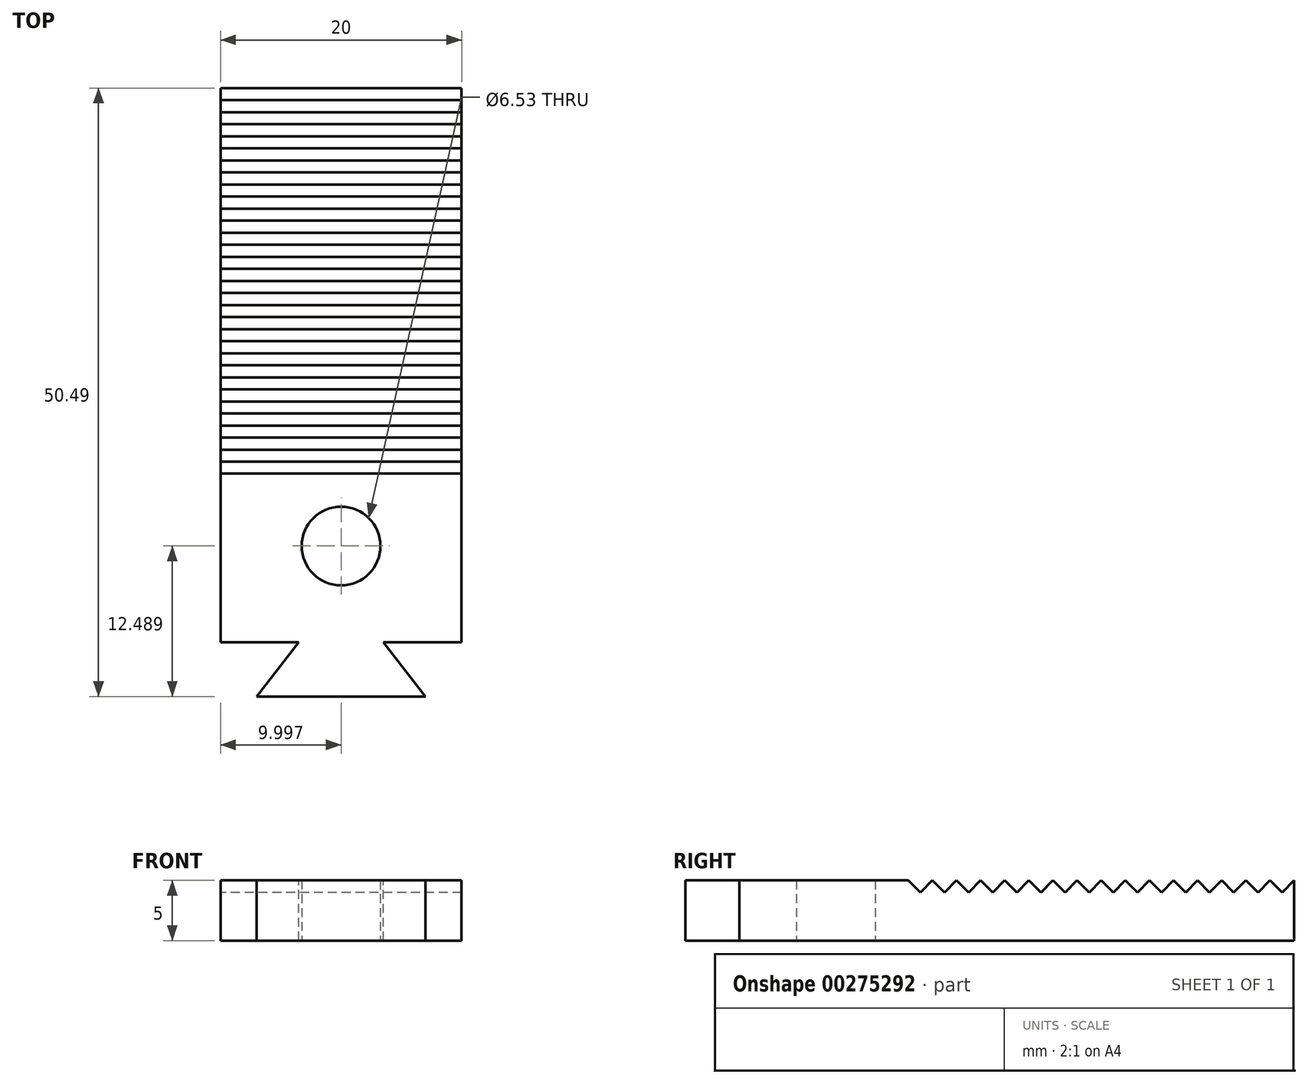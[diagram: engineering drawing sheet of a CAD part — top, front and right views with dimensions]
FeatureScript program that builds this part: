
annotation { "Feature Type Name" : "Feature", "Feature Type Description" : "" }
export const myFeature = defineFeature(function(context is Context, id is Id, definition is map)
    precondition{}
    {
        {
            var Q0;
            Q0=qCreatedBy(makeId("Top.planeOp"),FACE);
            var sketch = newSketch(context, id + "F0", { "sketchPlane" : qUnion([Q0])});
            skLineSegment(sketch, "E0.bottom", {"start": v(-15.11, 35.05) * mm, "end": v(4.89, 35.05) * mm});
            skLineSegment(sketch, "E0.top", {"start": v(-15.11, -20.95) * mm, "end": v(4.89, -20.95) * mm});
            skLineSegment(sketch, "E0.left", {"start": v(-15.11, 35.05) * mm, "end": v(-15.11, -20.95) * mm});
            skLineSegment(sketch, "E0.right", {"start": v(4.89, 35.05) * mm, "end": v(4.89, -20.95) * mm});
            skSolve(sketch);
        }
        {
            var Q0;
            Q0=makeQuery(id+"F0.imprint","IMPRINT",FACE,{"disambiguationData":[TD([[makeQuery(id+"F0.imprint","IMPRINT",EDGE,{"derivedFrom":sQuery(id+"F0.wireOp",EDGE,"E0.bottom")}),-1.0]])]});
            extrude(context, id + "F1", {"entities" : qUnion([Q0]), "depth" : 5 * mm});
        }
        {
            var Q0;
            Q0=makeQuery(id+"F1.opExtrude","CAP_FACE",FACE,{"disambiguationData":[OSD([sQuery(id+"F0.wireOp",EDGE,"E0.bottom"),sQuery(id+"F0.wireOp",EDGE,"E0.top"),sQuery(id+"F0.wireOp",EDGE,"E0.left"),sQuery(id+"F0.wireOp",EDGE,"E0.right")])],"isStart":false});
            var sketch = newSketch(context, id + "F2", { "sketchPlane" : qUnion([Q0])});
            skLineSegment(sketch, "E1.bottom", {"start": v(-15.11, -20.95) * mm, "end": v(4.89, -20.95) * mm});
            skLineSegment(sketch, "E1.top", {"start": v(-15.11, -10.95) * mm, "end": v(4.89, -10.95) * mm});
            skLineSegment(sketch, "E1.left", {"start": v(-15.11, -20.95) * mm, "end": v(-15.11, -10.95) * mm});
            skLineSegment(sketch, "E1.right", {"start": v(4.89, -20.95) * mm, "end": v(4.89, -10.95) * mm});
            skSolve(sketch);
        }
        {
            var Q0;
            Q0=makeQuery(id+"F2.imprint","IMPRINT",FACE,{"disambiguationData":[TD([[makeQuery(id+"F2.imprint","IMPRINT",EDGE,{"derivedFrom":sQuery(id+"F2.wireOp",EDGE,"E1.bottom")}),1.0]])]});
            extrude(context, id + "F3", {"entities" : qUnion([Q0]), "operationType" : NewBodyOperationType.ADD, "depth" : 45 * mm});
        }
        {
            var Q0;
            Q0=makeQuery(id+"F1.opExtrude","CAP_FACE",FACE,{"disambiguationData":[OSD([sQuery(id+"F0.wireOp",EDGE,"E0.bottom"),sQuery(id+"F0.wireOp",EDGE,"E0.top"),sQuery(id+"F0.wireOp",EDGE,"E0.left"),sQuery(id+"F0.wireOp",EDGE,"E0.right")])],"isStart":true});
            var sketch = newSketch(context, id + "F4", { "sketchPlane" : qUnion([Q0])});
            skPoint(sketch, "E2", {"position": v(-5.11, 2.95) * mm});
            skCircle(sketch, "E3.cCircle", {"center": v(-5.11, 2.95) * mm, "radius": 5.45 * mm, "construction": true});
            skLineSegment(sketch, "E3.0", {"start": v(-11.4, 2.95) * mm, "end": v(-8.26, 8.4) * mm});
            skLineSegment(sketch, "E3.1", {"start": v(-8.26, 8.4) * mm, "end": v(-1.97, 8.4) * mm});
            skLineSegment(sketch, "E3.2", {"start": v(-1.97, 8.4) * mm, "end": v(1.18, 2.95) * mm});
            skLineSegment(sketch, "E3.3", {"start": v(1.18, 2.95) * mm, "end": v(-1.97, -2.5) * mm});
            skLineSegment(sketch, "E3.4", {"start": v(-1.97, -2.5) * mm, "end": v(-8.26, -2.5) * mm});
            skLineSegment(sketch, "E3.5", {"start": v(-8.26, -2.5) * mm, "end": v(-11.4, 2.95) * mm});
            skPoint(sketch, "E3.0.midPoint", {"position": v(-9.83, 5.68) * mm});
            skSolve(sketch);
        }
        {
            var Q0;
            Q0=sQuery(id+"F4.wireOp",VERTEX,"E2");
            var Q1;
            Q1=makeQuery(id+"F1.opExtrude","SWEPT_BODY",BODY,{"disambiguationData":[OSD([sQuery(id+"F0.wireOp",EDGE,"E0.bottom"),sQuery(id+"F0.wireOp",EDGE,"E0.top"),sQuery(id+"F0.wireOp",EDGE,"E0.left"),sQuery(id+"F0.wireOp",EDGE,"E0.right")])]});
            hole(context, id + "F5", {"style" : HoleStyle.SIMPLE, "endStyle" : HoleEndStyle.THROUGH, "holeDiameter" : 6.53 * mm, "tappedDepth" : 12 * mm, "tapClearance" : 3, "locations" : qUnion([Q0]), "scope" : qUnion([Q1])});
        }
        {
            var Q0;
            Q0=makeQuery(id+"F3.boolean.opBoolean","MERGE",FACE,{"derivedFrom":[makeQuery(id+"F1.opExtrude","SWEPT_FACE",FACE,{"disambiguationData":[OSD([sQuery(id+"F0.wireOp",EDGE,"E0.left")])]}),makeQuery(id+"F3.opExtrude","SWEPT_FACE",FACE,{"disambiguationData":[OSD([sQuery(id+"F2.wireOp",EDGE,"E1.left")])]})]});
            var sketch = newSketch(context, id + "F6", { "sketchPlane" : qUnion([Q0])});
            skLineSegment(sketch, "E4", {"start": v(-35.05, 5) * mm, "end": v(-34.05, 4) * mm});
            skLineSegment(sketch, "E5", {"start": v(-34.05, 4) * mm, "end": v(-33.05, 5) * mm});
            skLineSegment(sketch, "E6", {"start": v(-33.05, 5) * mm, "end": v(-32.05, 4) * mm});
            skLineSegment(sketch, "E7", {"start": v(-32.05, 4) * mm, "end": v(-31.05, 5) * mm});
            skLineSegment(sketch, "E8", {"start": v(-31.05, 5) * mm, "end": v(-30.05, 4) * mm});
            skLineSegment(sketch, "E9", {"start": v(-30.05, 4) * mm, "end": v(-29.05, 5) * mm});
            skLineSegment(sketch, "E10", {"start": v(-29.05, 5) * mm, "end": v(-28.05, 4) * mm});
            skLineSegment(sketch, "E11", {"start": v(-28.05, 4) * mm, "end": v(-27.05, 5) * mm});
            skLineSegment(sketch, "E12", {"start": v(-27.05, 5) * mm, "end": v(-26.05, 4) * mm});
            skLineSegment(sketch, "E13", {"start": v(-26.05, 4) * mm, "end": v(-25.05, 5) * mm});
            skLineSegment(sketch, "E14", {"start": v(-25.05, 5) * mm, "end": v(-24.05, 4) * mm});
            skLineSegment(sketch, "E15", {"start": v(-24.05, 4) * mm, "end": v(-23.05, 5) * mm});
            skLineSegment(sketch, "E16", {"start": v(-23.05, 5) * mm, "end": v(-22.05, 4) * mm});
            skLineSegment(sketch, "E17", {"start": v(-22.05, 4) * mm, "end": v(-21.05, 5) * mm});
            skLineSegment(sketch, "E18", {"start": v(-21.05, 5) * mm, "end": v(-20.05, 4) * mm});
            skLineSegment(sketch, "E19", {"start": v(-20.05, 4) * mm, "end": v(-19.05, 5) * mm});
            skLineSegment(sketch, "E20", {"start": v(-19.05, 5) * mm, "end": v(-18.05, 4) * mm});
            skLineSegment(sketch, "E21", {"start": v(-18.05, 4) * mm, "end": v(-17.05, 5) * mm});
            skLineSegment(sketch, "E22", {"start": v(-17.05, 5) * mm, "end": v(-16.05, 4) * mm});
            skLineSegment(sketch, "E23", {"start": v(-16.05, 4) * mm, "end": v(-15.05, 5) * mm});
            skLineSegment(sketch, "E24", {"start": v(-15.05, 5) * mm, "end": v(-14.05, 4) * mm});
            skLineSegment(sketch, "E25", {"start": v(-14.05, 4) * mm, "end": v(-13.05, 5) * mm});
            skLineSegment(sketch, "E26", {"start": v(-13.05, 5) * mm, "end": v(-12.05, 4) * mm});
            skLineSegment(sketch, "E27", {"start": v(-12.05, 4) * mm, "end": v(-11.05, 5) * mm});
            skLineSegment(sketch, "E28", {"start": v(-11.05, 5) * mm, "end": v(-10.05, 4) * mm});
            skLineSegment(sketch, "E29", {"start": v(-10.05, 4) * mm, "end": v(-9.05, 5) * mm});
            skLineSegment(sketch, "E30", {"start": v(-9.05, 5) * mm, "end": v(-8.05, 4) * mm});
            skLineSegment(sketch, "E31", {"start": v(-8.05, 4) * mm, "end": v(-7.05, 5) * mm});
            skLineSegment(sketch, "E32", {"start": v(-7.05, 5) * mm, "end": v(-6.05, 4) * mm});
            skLineSegment(sketch, "E33", {"start": v(-6.05, 4) * mm, "end": v(-5.05, 5) * mm});
            skLineSegment(sketch, "E34", {"start": v(-5.05, 5) * mm, "end": v(-4.05, 4) * mm});
            skLineSegment(sketch, "E35", {"start": v(-4.05, 4) * mm, "end": v(-3.05, 5) * mm});
            skSolve(sketch);
        }
        {
            var Q0;
            {var subQ0=sQuery(id+"F6.wireOp",EDGE,"E4");Q0=makeQuery(id+"F6.imprint","IMPRINT",FACE,{"disambiguationData":[TD([[makeQuery(id+"F6.imprint","IMPRINT",EDGE,{"derivedFrom":subQ0}),1.0]])]});}
            var Q1;
            {var subQ0=sQuery(id+"F6.wireOp",EDGE,"E6");Q1=makeQuery(id+"F6.imprint","IMPRINT",FACE,{"disambiguationData":[TD([[makeQuery(id+"F6.imprint","IMPRINT",EDGE,{"derivedFrom":subQ0}),1.0]])]});}
            var Q2;
            {var subQ0=sQuery(id+"F6.wireOp",EDGE,"E8");Q2=makeQuery(id+"F6.imprint","IMPRINT",FACE,{"disambiguationData":[TD([[makeQuery(id+"F6.imprint","IMPRINT",EDGE,{"derivedFrom":subQ0}),1.0]])]});}
            var Q3;
            {var subQ0=sQuery(id+"F6.wireOp",EDGE,"E10");Q3=makeQuery(id+"F6.imprint","IMPRINT",FACE,{"disambiguationData":[TD([[makeQuery(id+"F6.imprint","IMPRINT",EDGE,{"derivedFrom":subQ0}),1.0]])]});}
            var Q4;
            {var subQ0=sQuery(id+"F6.wireOp",EDGE,"E12");Q4=makeQuery(id+"F6.imprint","IMPRINT",FACE,{"disambiguationData":[TD([[makeQuery(id+"F6.imprint","IMPRINT",EDGE,{"derivedFrom":subQ0}),1.0]])]});}
            var Q5;
            {var subQ0=sQuery(id+"F6.wireOp",EDGE,"E14");Q5=makeQuery(id+"F6.imprint","IMPRINT",FACE,{"disambiguationData":[TD([[makeQuery(id+"F6.imprint","IMPRINT",EDGE,{"derivedFrom":subQ0}),1.0]])]});}
            var Q6;
            {var subQ0=sQuery(id+"F6.wireOp",EDGE,"E16");Q6=makeQuery(id+"F6.imprint","IMPRINT",FACE,{"disambiguationData":[TD([[makeQuery(id+"F6.imprint","IMPRINT",EDGE,{"derivedFrom":subQ0}),1.0]])]});}
            var Q7;
            {var subQ0=sQuery(id+"F6.wireOp",EDGE,"E18");Q7=makeQuery(id+"F6.imprint","IMPRINT",FACE,{"disambiguationData":[TD([[makeQuery(id+"F6.imprint","IMPRINT",EDGE,{"derivedFrom":subQ0}),1.0]])]});}
            var Q8;
            {var subQ0=sQuery(id+"F6.wireOp",EDGE,"E20");Q8=makeQuery(id+"F6.imprint","IMPRINT",FACE,{"disambiguationData":[TD([[makeQuery(id+"F6.imprint","IMPRINT",EDGE,{"derivedFrom":subQ0}),1.0]])]});}
            var Q9;
            {var subQ0=sQuery(id+"F6.wireOp",EDGE,"E22");Q9=makeQuery(id+"F6.imprint","IMPRINT",FACE,{"disambiguationData":[TD([[makeQuery(id+"F6.imprint","IMPRINT",EDGE,{"derivedFrom":subQ0}),1.0]])]});}
            var Q10;
            {var subQ0=sQuery(id+"F6.wireOp",EDGE,"E24");Q10=makeQuery(id+"F6.imprint","IMPRINT",FACE,{"disambiguationData":[TD([[makeQuery(id+"F6.imprint","IMPRINT",EDGE,{"derivedFrom":subQ0}),1.0]])]});}
            var Q11;
            {var subQ0=sQuery(id+"F6.wireOp",EDGE,"E26");Q11=makeQuery(id+"F6.imprint","IMPRINT",FACE,{"disambiguationData":[TD([[makeQuery(id+"F6.imprint","IMPRINT",EDGE,{"derivedFrom":subQ0}),1.0]])]});}
            var Q12;
            {var subQ0=sQuery(id+"F6.wireOp",EDGE,"E28");Q12=makeQuery(id+"F6.imprint","IMPRINT",FACE,{"disambiguationData":[TD([[makeQuery(id+"F6.imprint","IMPRINT",EDGE,{"derivedFrom":subQ0}),1.0]])]});}
            var Q13;
            {var subQ0=sQuery(id+"F6.wireOp",EDGE,"E30");Q13=makeQuery(id+"F6.imprint","IMPRINT",FACE,{"disambiguationData":[TD([[makeQuery(id+"F6.imprint","IMPRINT",EDGE,{"derivedFrom":subQ0}),1.0]])]});}
            var Q14;
            {var subQ0=sQuery(id+"F6.wireOp",EDGE,"E32");Q14=makeQuery(id+"F6.imprint","IMPRINT",FACE,{"disambiguationData":[TD([[makeQuery(id+"F6.imprint","IMPRINT",EDGE,{"derivedFrom":subQ0}),1.0]])]});}
            var Q15;
            {var subQ0=sQuery(id+"F6.wireOp",EDGE,"E34");Q15=makeQuery(id+"F6.imprint","IMPRINT",FACE,{"disambiguationData":[TD([[makeQuery(id+"F6.imprint","IMPRINT",EDGE,{"derivedFrom":subQ0}),1.0]])]});}
            extrude(context, id + "F7", {"entities" : qUnion([Q0, Q1, Q2, Q3, Q4, Q5, Q6, Q7, Q8, Q9, Q10, Q11, Q12, Q13, Q14, Q15]), "operationType" : NewBodyOperationType.REMOVE, "endBound" : BoundingType.UP_TO_NEXT, "oppositeDirection" : true, "depth" : 25 * mm});
        }
        {
            var Q0;
            Q0=makeQuery(id+"F3.opExtrude","CAP_FACE",FACE,{"disambiguationData":[OSD([sQuery(id+"F2.wireOp",EDGE,"E1.bottom"),sQuery(id+"F2.wireOp",EDGE,"E1.top"),sQuery(id+"F2.wireOp",EDGE,"E1.left"),sQuery(id+"F2.wireOp",EDGE,"E1.right")])],"isStart":false});
            var sketch = newSketch(context, id + "F8", { "sketchPlane" : qUnion([Q0])});
            skLineSegment(sketch, "E36", {"start": v(-8.61, -10.95) * mm, "end": v(-1.61, -10.95) * mm});
            skLineSegment(sketch, "E37", {"start": v(-12.11, -15.44) * mm, "end": v(1.89, -15.44) * mm});
            skLineSegment(sketch, "E38", {"start": v(1.89, -15.44) * mm, "end": v(-1.61, -10.95) * mm});
            skLineSegment(sketch, "E39", {"start": v(-12.11, -15.44) * mm, "end": v(-8.61, -10.95) * mm});
            skSolve(sketch);
        }
        {
            var Q0;
            Q0=makeQuery(id+"F8.imprint","IMPRINT",FACE,{"disambiguationData":[TD([[makeQuery(id+"F8.imprint","IMPRINT",EDGE,{"derivedFrom":sQuery(id+"F8.wireOp",EDGE,"E36")}),-1.0]])]});
            extrude(context, id + "F9", {"entities" : qUnion([Q0]), "operationType" : NewBodyOperationType.REMOVE, "oppositeDirection" : true, "depth" : 45 * mm});
        }
        {
            var Q0;
            Q0=makeQuery(id+"F3.opExtrude","CAP_FACE",FACE,{"disambiguationData":[OSD([sQuery(id+"F2.wireOp",EDGE,"E1.bottom"),sQuery(id+"F2.wireOp",EDGE,"E1.top"),sQuery(id+"F2.wireOp",EDGE,"E1.left"),sQuery(id+"F2.wireOp",EDGE,"E1.right")])],"isStart":false});
            extrude(context, id + "F10", {"entities" : qUnion([Q0]), "operationType" : NewBodyOperationType.REMOVE, "endBound" : BoundingType.THROUGH_ALL, "oppositeDirection" : true, "depth" : 25 * mm});
        }
    });
